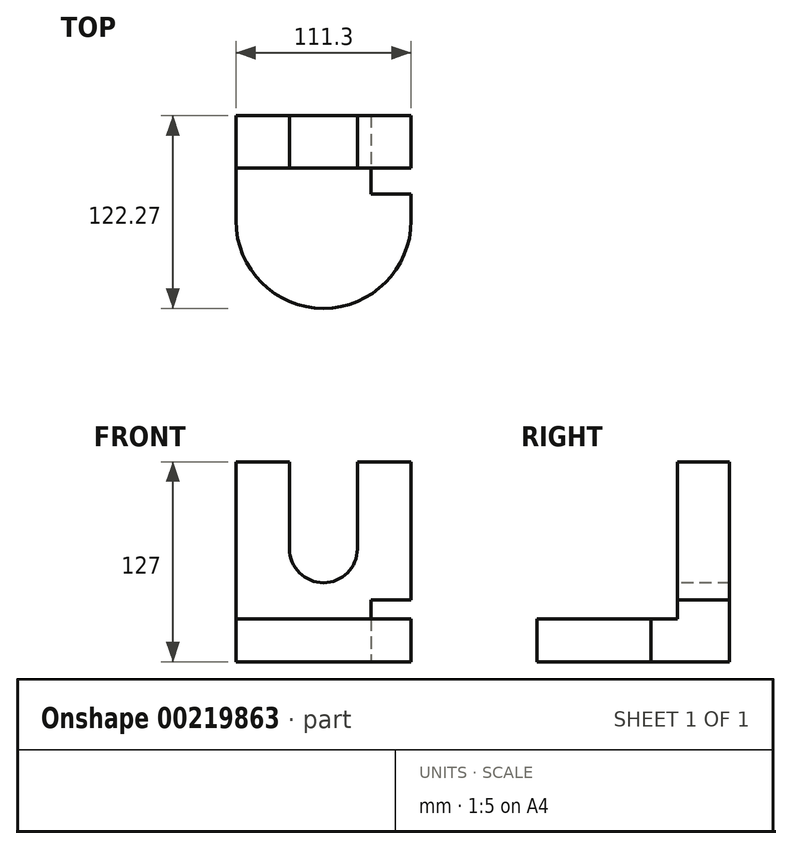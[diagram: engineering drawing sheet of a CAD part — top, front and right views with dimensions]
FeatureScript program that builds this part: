
annotation { "Feature Type Name" : "Feature", "Feature Type Description" : "" }
export const myFeature = defineFeature(function(context is Context, id is Id, definition is map)
    precondition{}
    {
        {
            var Q0;
            Q0=qCreatedBy(makeId("Top.planeOp"),FACE);
            var sketch = newSketch(context, id + "F0", { "sketchPlane" : qUnion([Q0])});
            skLineSegment(sketch, "E0.bottom", {"start": v(55.65, 66.62) * mm, "end": v(-55.65, 66.62) * mm});
            skLineSegment(sketch, "E0.top", {"start": v(55.65, -66.62) * mm, "end": v(-55.65, -66.62) * mm});
            skLineSegment(sketch, "E0.left", {"start": v(55.65, 66.62) * mm, "end": v(55.65, -66.62) * mm});
            skLineSegment(sketch, "E0.right", {"start": v(-55.65, 66.62) * mm, "end": v(-55.65, -66.62) * mm});
            skPoint(sketch, "E0.middle", {"position": v(0, 0) * mm});
            skSolve(sketch);
        }
        {
            var Q0;
            Q0 = qSketchRegion(id + "F0", true);
            extrude(context, id + "F1", {"entities" : qUnion([Q0]), "depth" : 127 * mm});
        }
        {
            var Q0;
            Q0=makeQuery(id+"F1.opExtrude","SWEPT_FACE",FACE,{"disambiguationData":[OSD([sQuery(id+"F0.wireOp",EDGE,"E0.left")])]});
            var sketch = newSketch(context, id + "F2", { "sketchPlane" : qUnion([Q0])});
            skLineSegment(sketch, "E1", {"start": v(-66.62, 127) * mm, "end": v(33.56, 127) * mm});
            skLineSegment(sketch, "E2", {"start": v(33.56, 127) * mm, "end": v(33.56, 27.1) * mm});
            skLineSegment(sketch, "E3", {"start": v(33.56, 27.1) * mm, "end": v(-66.62, 27.1) * mm});
            skLineSegment(sketch, "E4", {"start": v(-66.62, 27.1) * mm, "end": v(-66.62, 127) * mm});
            skSolve(sketch);
        }
        {
            var Q0;
            Q0=makeQuery(id+"F2.imprint","IMPRINT",FACE,{"disambiguationData":[TD([[makeQuery(id+"F2.imprint","IMPRINT",EDGE,{"derivedFrom":sQuery(id+"F2.wireOp",EDGE,"E1")}),1.0]])]});
            extrude(context, id + "F3", {"entities" : qUnion([Q0]), "operationType" : NewBodyOperationType.REMOVE, "oppositeDirection" : true, "depth" : 116.6 * mm});
        }
        {
            var Q0;
            Q0=makeQuery(id+"F3.boolean.opBoolean","COPY",FACE,{"derivedFrom":makeQuery(id+"F3.opExtrude","SWEPT_FACE",FACE,{"disambiguationData":[OSD([sQuery(id+"F2.wireOp",EDGE,"E3")])]})});
            var sketch = newSketch(context, id + "F4", { "sketchPlane" : qUnion([Q0])});
            skArc(sketch, "E5", {"start": v(-55.65, 0) * mm, "mid": v(0, -55.65) * mm, "end": v(55.65, 0) * mm});
            skLineSegment(sketch, "E6", {"start": v(-55.65, 0) * mm, "end": v(-55.65, -66.62) * mm});
            skLineSegment(sketch, "E7", {"start": v(-55.65, -66.62) * mm, "end": v(55.65, -66.62) * mm});
            skLineSegment(sketch, "E8", {"start": v(55.65, -66.62) * mm, "end": v(55.65, 0) * mm});
            skSolve(sketch);
        }
        {
            var Q0;
            Q0 = qSketchRegion(id + "F4", true);
            extrude(context, id + "F5", {"entities" : qUnion([Q0]), "operationType" : NewBodyOperationType.REMOVE, "oppositeDirection" : true, "depth" : 49.28 * mm});
        }
        {
            var Q0;
            Q0=makeQuery(id+"F3.boolean.opBoolean","COPY",FACE,{"derivedFrom":makeQuery(id+"F3.opExtrude","SWEPT_FACE",FACE,{"disambiguationData":[OSD([sQuery(id+"F2.wireOp",EDGE,"E2")])]})});
            var sketch = newSketch(context, id + "F6", { "sketchPlane" : qUnion([Q0])});
            skLineSegment(sketch, "E9", {"start": v(-55.65, 127) * mm, "end": v(55.65, 127) * mm});
            skLineSegment(sketch, "E10.left", {"start": v(21.55, 71.74) * mm, "end": v(21.55, 127) * mm});
            skLineSegment(sketch, "E10.right", {"start": v(-21.55, 71.74) * mm, "end": v(-21.55, 127) * mm});
            skPoint(sketch, "E10.middle", {"position": v(0, 127) * mm});
            skArc(sketch, "E11", {"start": v(-21.55, 71.74) * mm, "mid": v(0, 50.18) * mm, "end": v(21.55, 71.74) * mm});
            skPoint(sketch, "E12.orphan", {"position": v(-21.55, 182.26) * mm});
            skPoint(sketch, "E13.orphan", {"position": v(21.55, 182.26) * mm});
            skLineSegment(sketch, "E14", {"start": v(-21.55, 127) * mm, "end": v(21.55, 127) * mm});
            skSolve(sketch);
        }
        {
            var Q0;
            Q0=makeQuery(id+"F6.imprint","IMPRINT",FACE,{"disambiguationData":[TD([[makeQuery(id+"F6.imprint","IMPRINT",EDGE,{"derivedFrom":sQuery(id+"F6.wireOp",EDGE,"E10.left")}),1.0]])]});
            extrude(context, id + "F7", {"entities" : qUnion([Q0]), "operationType" : NewBodyOperationType.REMOVE, "oppositeDirection" : true, "depth" : 54.6 * mm});
        }
        {
            var Q0;
            Q0=makeQuery(id+"F1.opExtrude","SWEPT_FACE",FACE,{"disambiguationData":[OSD([sQuery(id+"F0.wireOp",EDGE,"E0.left")])]});
            var sketch = newSketch(context, id + "F8", { "sketchPlane" : qUnion([Q0])});
            skLineSegment(sketch, "E15", {"start": v(16.78, 27.1) * mm, "end": v(16.78, 0) * mm});
            skLineSegment(sketch, "E16", {"start": v(16.78, 0) * mm, "end": v(66.62, 0) * mm});
            skLineSegment(sketch, "E17", {"start": v(66.62, 0) * mm, "end": v(66.62, 39.1) * mm});
            skLineSegment(sketch, "E18", {"start": v(66.62, 39.1) * mm, "end": v(29.25, 39.1) * mm});
            skLineSegment(sketch, "E19", {"start": v(29.25, 39.1) * mm, "end": v(29.25, 29.56) * mm});
            skLineSegment(sketch, "E20", {"start": v(29.25, 29.56) * mm, "end": v(16.78, 27.1) * mm});
            skSolve(sketch);
        }
        {
            var Q0;
            Q0 = qSketchRegion(id + "F8", true);
            extrude(context, id + "F9", {"entities" : qUnion([Q0]), "operationType" : NewBodyOperationType.REMOVE, "oppositeDirection" : true, "depth" : 25.4 * mm});
        }
    });
